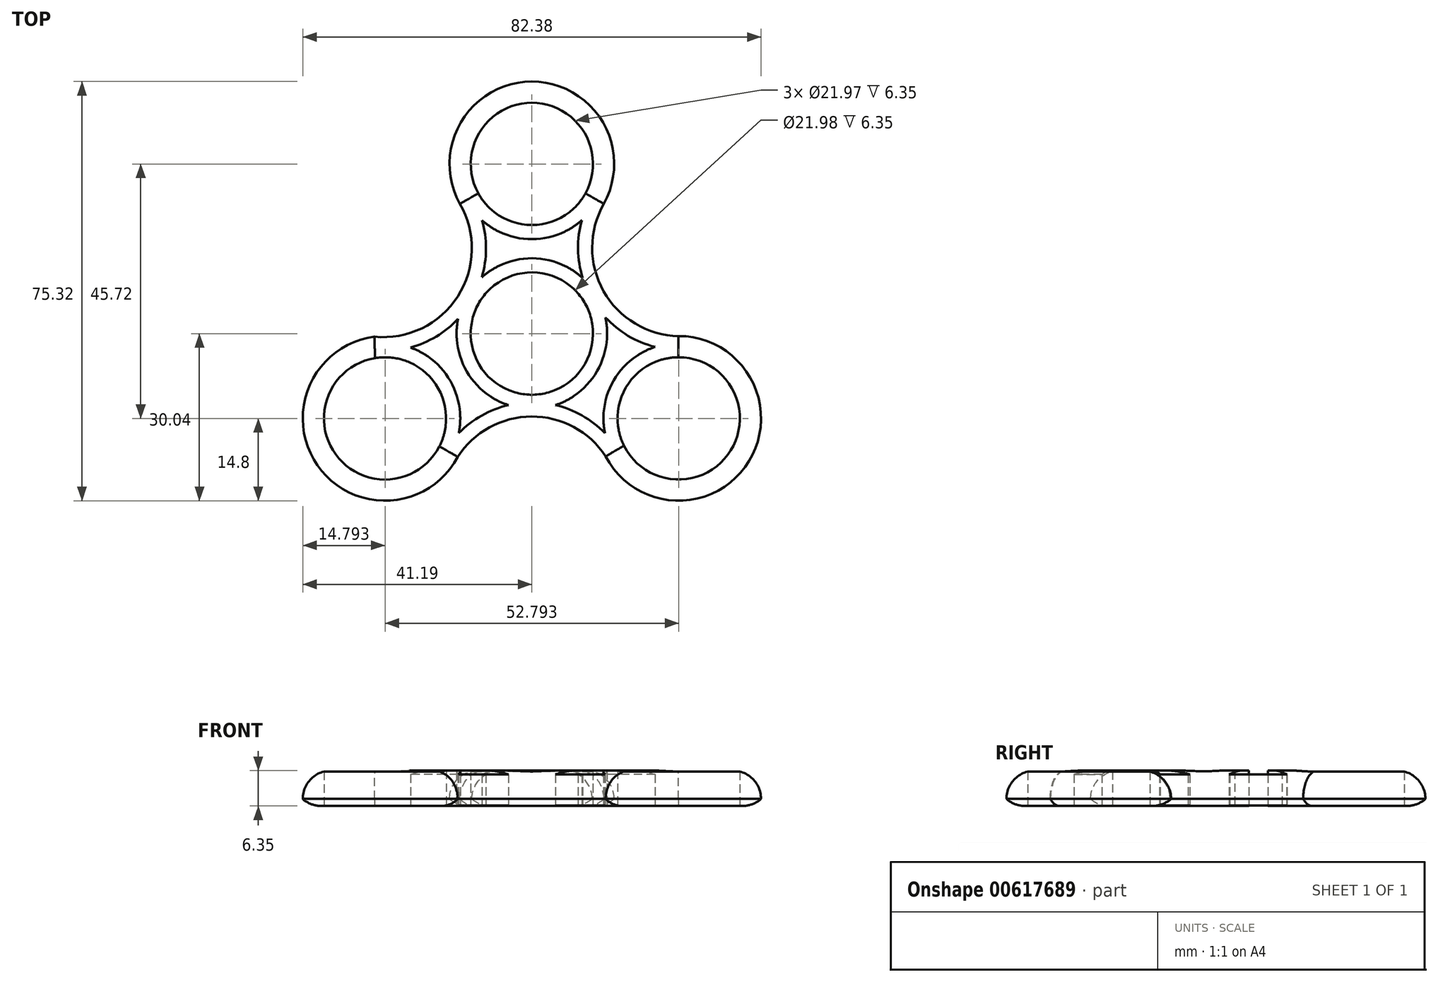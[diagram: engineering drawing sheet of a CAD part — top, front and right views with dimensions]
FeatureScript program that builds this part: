
annotation { "Feature Type Name" : "Feature", "Feature Type Description" : "" }
export const myFeature = defineFeature(function(context is Context, id is Id, definition is map)
    precondition{}
    {
        {
            var Q0;
            Q0=qCreatedBy(makeId("Top.planeOp"),FACE);
            var sketch = newSketch(context, id + "F0", { "sketchPlane" : qUnion([Q0])});
            skCircle(sketch, "E0", {"center": v(0, 0) * mm, "radius": 11 * mm});
            skLineSegment(sketch, "E1", {"start": v(0, 0) * mm, "end": v(0, 30.48) * mm});
            skLineSegment(sketch, "E2", {"start": v(0, 0) * mm, "end": v(-26.4, -15.24) * mm});
            skLineSegment(sketch, "E3", {"start": v(0, 0) * mm, "end": v(26.4, -15.24) * mm});
            skCircle(sketch, "E4", {"center": v(0, 30.48) * mm, "radius": 10.99 * mm});
            skCircle(sketch, "E5", {"center": v(-26.4, -15.24) * mm, "radius": 10.99 * mm});
            skCircle(sketch, "E6", {"center": v(26.4, -15.24) * mm, "radius": 10.99 * mm});
            skCircle(sketch, "E7", {"center": v(0, 30.48) * mm, "radius": 14.8 * mm});
            skCircle(sketch, "E8", {"center": v(-26.4, -15.24) * mm, "radius": 14.8 * mm});
            skCircle(sketch, "E9", {"center": v(26.4, -15.24) * mm, "radius": 14.8 * mm});
            skCircle(sketch, "E10", {"center": v(0, 0) * mm, "radius": 14.8 * mm});
            skArc(sketch, "E11", {"start": v(12.94, 23.3) * mm, "mid": v(12.9, 7.62) * mm, "end": v(26.36, -0.44) * mm});
            skArc(sketch, "E12", {"start": v(-28.29, -0.57) * mm, "mid": v(-13.32, 6.68) * mm, "end": v(-12.94, 23.3) * mm});
            skArc(sketch, "E13", {"start": v(13.27, -22.07) * mm, "mid": v(-0.05, -14.9) * mm, "end": v(-13.32, -22.17) * mm});
            skSolve(sketch);
        }
        {
            var Q0;
            {var subQ0=sQuery(id+"F0.wireOp",EDGE,"E2");var subQ1=sQuery(id+"F0.wireOp",EDGE,"E0");var subQ2=makeQuery(id+"F0.imprint","INTERSECT",VERTEX,{"derivedFrom":[subQ1,subQ0]});Q0=makeQuery(id+"F0.imprint","IMPRINT",FACE,{"disambiguationData":[TD([[makeQuery(id+"F0.imprint","IMPRINT",EDGE,{"disambiguationData":[TD([[subQ2,1.0]])],"derivedFrom":subQ1}),-1.0]])]});}
            var Q1;
            {var subQ0=sQuery(id+"F0.wireOp",EDGE,"E2");var subQ1=sQuery(id+"F0.wireOp",EDGE,"E0");var subQ2=makeQuery(id+"F0.imprint","INTERSECT",VERTEX,{"derivedFrom":[subQ1,subQ0]});Q1=makeQuery(id+"F0.imprint","IMPRINT",FACE,{"disambiguationData":[TD([[makeQuery(id+"F0.imprint","IMPRINT",EDGE,{"disambiguationData":[TD([[subQ2,-1.0]])],"derivedFrom":subQ1}),-1.0]])]});}
            var Q2;
            {var subQ0=sQuery(id+"F0.wireOp",EDGE,"E13");Q2=makeQuery(id+"F0.imprint","IMPRINT",FACE,{"disambiguationData":[TD([[makeQuery(id+"F0.imprint","IMPRINT",EDGE,{"derivedFrom":subQ0}),-1.0]])]});}
            var Q3;
            Q3=makeQuery(id+"F0.imprint","IMPRINT",FACE,{"disambiguationData":[TD([[makeQuery(id+"F0.imprint","IMPRINT",EDGE,{"derivedFrom":sQuery(id+"F0.wireOp",EDGE,"E5")}),-1.0]])]});
            var Q4;
            Q4=makeQuery(id+"F0.imprint","IMPRINT",FACE,{"disambiguationData":[TD([[makeQuery(id+"F0.imprint","IMPRINT",EDGE,{"derivedFrom":sQuery(id+"F0.wireOp",EDGE,"E6")}),-1.0]])]});
            var Q5;
            {var subQ0=sQuery(id+"F0.wireOp",EDGE,"E1");var subQ1=sQuery(id+"F0.wireOp",EDGE,"E0");var subQ2=makeQuery(id+"F0.imprint","INTERSECT",VERTEX,{"derivedFrom":[subQ1,subQ0]});Q5=makeQuery(id+"F0.imprint","IMPRINT",FACE,{"disambiguationData":[TD([[makeQuery(id+"F0.imprint","IMPRINT",EDGE,{"disambiguationData":[TD([[subQ2,1.0]])],"derivedFrom":subQ1}),-1.0]])]});}
            var Q6;
            {var subQ5=sQuery(id+"F0.wireOp",EDGE,"E7");var subQ6=sQuery(id+"F0.wireOp",EDGE,"E1");var subQ7=makeQuery(id+"F0.imprint","INTERSECT",VERTEX,{"derivedFrom":[subQ6,subQ5]});Q6=makeQuery(id+"F0.imprint","IMPRINT",FACE,{"disambiguationData":[TD([[makeQuery(id+"F0.imprint","IMPRINT",EDGE,{"disambiguationData":[TD([[subQ7,1.0]])],"derivedFrom":subQ6}),-1.0]])]});}
            var Q7;
            {var subQ0=sQuery(id+"F0.wireOp",EDGE,"E7");var subQ1=sQuery(id+"F0.wireOp",EDGE,"E1");var subQ2=makeQuery(id+"F0.imprint","INTERSECT",VERTEX,{"derivedFrom":[subQ1,subQ0]});Q7=makeQuery(id+"F0.imprint","IMPRINT",FACE,{"disambiguationData":[TD([[makeQuery(id+"F0.imprint","IMPRINT",EDGE,{"disambiguationData":[TD([[subQ2,1.0]])],"derivedFrom":subQ1}),1.0]])]});}
            var Q8;
            Q8=makeQuery(id+"F0.imprint","IMPRINT",FACE,{"disambiguationData":[TD([[makeQuery(id+"F0.imprint","IMPRINT",EDGE,{"derivedFrom":sQuery(id+"F0.wireOp",EDGE,"E4")}),-1.0]])]});
            extrude(context, id + "F1", {"entities" : qUnion([Q0, Q1, Q2, Q3, Q4, Q5, Q6, Q7, Q8]), "depth" : 6.35 * mm, "offsetDistance" : 25.4 * mm});
        }
        {
            var Q0;
            Q0=makeQuery(id+"F3.opFillet","SPLIT",FACE,{"disambiguationData":[OD(2.0)],"derivedFrom":makeQuery(id+"F1.opExtrude","CAP_FACE",FACE,{"disambiguationData":[OSD([sQuery(id+"F0.wireOp",EDGE,"E0"),sQuery(id+"F0.wireOp",EDGE,"E4"),sQuery(id+"F0.wireOp",EDGE,"E5"),sQuery(id+"F0.wireOp",EDGE,"E6"),sQuery(id+"F0.wireOp",EDGE,"E7"),sQuery(id+"F0.wireOp",EDGE,"E8"),sQuery(id+"F0.wireOp",EDGE,"E9"),sQuery(id+"F0.wireOp",EDGE,"E11"),sQuery(id+"F0.wireOp",EDGE,"E12"),sQuery(id+"F0.wireOp",EDGE,"E13")])],"isStart":false})});
            var Q1;
            Q1=makeQuery(id+"F1.opExtrude","CAP_FACE",FACE,{"disambiguationData":[OSD([sQuery(id+"F0.wireOp",EDGE,"E0"),sQuery(id+"F0.wireOp",EDGE,"E4"),sQuery(id+"F0.wireOp",EDGE,"E5"),sQuery(id+"F0.wireOp",EDGE,"E6"),sQuery(id+"F0.wireOp",EDGE,"E7"),sQuery(id+"F0.wireOp",EDGE,"E8"),sQuery(id+"F0.wireOp",EDGE,"E9"),sQuery(id+"F0.wireOp",EDGE,"E11"),sQuery(id+"F0.wireOp",EDGE,"E12"),sQuery(id+"F0.wireOp",EDGE,"E13")])],"isStart":true});
            shell(context, id + "F2", {"entities" : qUnion([Q0, Q1]), "thickness" : 2.54 * mm});
        }
        {
            var Q0;
            Q0=makeQuery(id+"F1.opExtrude","CAP_EDGE",EDGE,{"disambiguationData":[OSD([sQuery(id+"F0.wireOp",EDGE,"E7")])],"isStart":false});
            var Q1;
            Q1=makeQuery(id+"F1.opExtrude","CAP_EDGE",EDGE,{"disambiguationData":[OSD([sQuery(id+"F0.wireOp",EDGE,"E11")])],"isStart":false});
            var Q2;
            Q2=makeQuery(id+"F1.opExtrude","CAP_EDGE",EDGE,{"disambiguationData":[OSD([sQuery(id+"F0.wireOp",EDGE,"E9")])],"isStart":false});
            var Q3;
            Q3=makeQuery(id+"F1.opExtrude","CAP_EDGE",EDGE,{"disambiguationData":[OSD([sQuery(id+"F0.wireOp",EDGE,"E13")])],"isStart":false});
            var Q4;
            Q4=makeQuery(id+"F1.opExtrude","CAP_EDGE",EDGE,{"disambiguationData":[OSD([sQuery(id+"F0.wireOp",EDGE,"E8")])],"isStart":false});
            var Q5;
            Q5=makeQuery(id+"F1.opExtrude","CAP_EDGE",EDGE,{"disambiguationData":[OSD([sQuery(id+"F0.wireOp",EDGE,"E12")])],"isStart":false});
            fillet(context, id + "F3", {"entities" : qUnion([Q0, Q1, Q2, Q3, Q4, Q5]), "radius" : 5.08 * mm, "tangentPropagation" : true, "allowEdgeOverflow" : false});
        }
        {
            var Q0;
            Q0=makeQuery(id+"F1.opExtrude","CAP_EDGE",EDGE,{"disambiguationData":[OSD([sQuery(id+"F0.wireOp",EDGE,"E9")])],"isStart":true});
            var Q1;
            Q1=makeQuery(id+"F1.opExtrude","CAP_EDGE",EDGE,{"disambiguationData":[OSD([sQuery(id+"F0.wireOp",EDGE,"E13")])],"isStart":true});
            var Q2;
            Q2=makeQuery(id+"F1.opExtrude","CAP_EDGE",EDGE,{"disambiguationData":[OSD([sQuery(id+"F0.wireOp",EDGE,"E8")])],"isStart":true});
            var Q3;
            Q3=makeQuery(id+"F1.opExtrude","CAP_EDGE",EDGE,{"disambiguationData":[OSD([sQuery(id+"F0.wireOp",EDGE,"E12")])],"isStart":true});
            var Q4;
            Q4=makeQuery(id+"F1.opExtrude","CAP_EDGE",EDGE,{"disambiguationData":[OSD([sQuery(id+"F0.wireOp",EDGE,"E7")])],"isStart":true});
            var Q5;
            Q5=makeQuery(id+"F1.opExtrude","CAP_EDGE",EDGE,{"disambiguationData":[OSD([sQuery(id+"F0.wireOp",EDGE,"E11")])],"isStart":true});
            fillet(context, id + "F4", {"entities" : qUnion([Q0, Q1, Q2, Q3, Q4, Q5]), "radius" : 5.08 * mm, "tangentPropagation" : true, "allowEdgeOverflow" : false});
        }
    });
